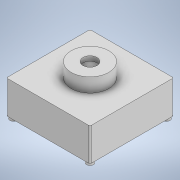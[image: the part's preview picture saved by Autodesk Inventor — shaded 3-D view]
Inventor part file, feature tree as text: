
AUTODESK INVENTOR PART (.ipt)
format: ipt  version: 2021 (Build 250183000, 183)  size: 144,384 bytes
history: native  units: mm
features: extrude x4, sketch x4, fillet x1
ambient origin geometry x8: Origin, YZ Plane, XZ Plane, XY Plane, X Axis, Y Axis, Z Axis, Center Point
bodies: Solid1 (feature_tree)
feature tree (9):
  extrude  "Extrusion1"  Depth=178.0mm
  extrude  "Extrusion2"  Depth=178.0mm
  extrude  "Extrusion3"  Depth=70.0mm
  extrude  "Extrusion4"  Depth=30.0mm
  fillet  "Fillet1"  Radius=10.0mm
  sketch  "Sketch1"  dims[d0=89.0mm d1=178.0mm]
  sketch  "Sketch2"  dims[d2=178.0mm d3=89.0mm]
  sketch  "Sketch3"  dims[d4=70.0mm d5=0.0mm d6=80.0mm]
  sketch  "Sketch4"  dims[d7=30.0mm d8=0.0mm d9=30.0mm d10=10.0mm d11=0.0mm d12=15.0mm d13=7.5mm d14=7.5mm d15=40.0mm d17=360.0deg d19=5.0mm d20=0.0mm d21=3.0mm]
